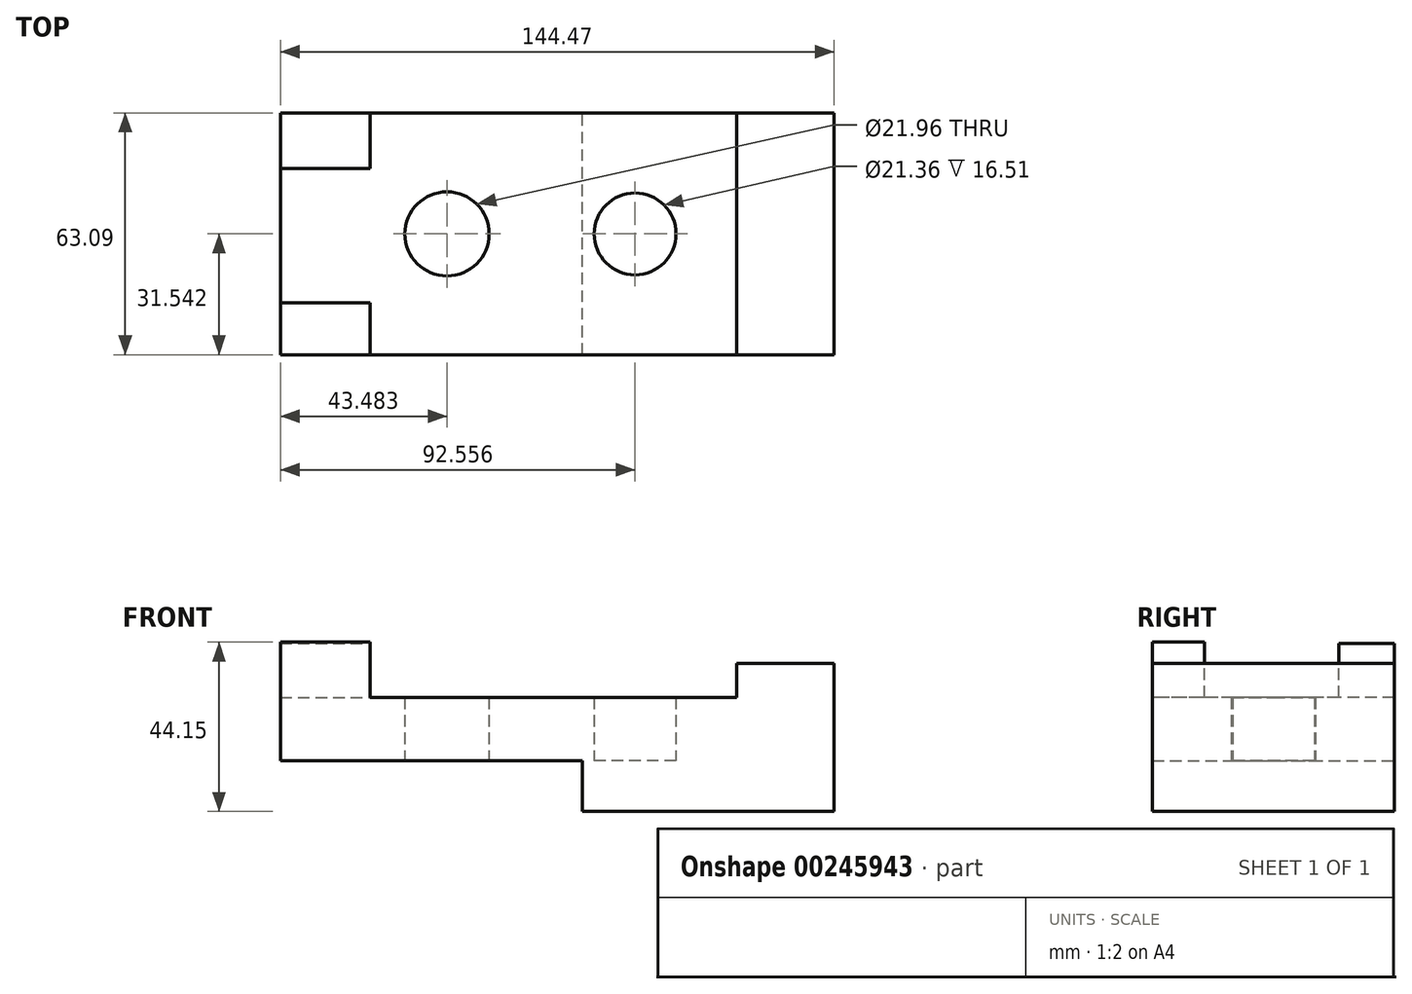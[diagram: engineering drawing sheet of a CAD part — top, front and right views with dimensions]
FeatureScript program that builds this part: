
annotation { "Feature Type Name" : "Feature", "Feature Type Description" : "" }
export const myFeature = defineFeature(function(context is Context, id is Id, definition is map)
    precondition{}
    {
        {
            var Q0;
            Q0=qCreatedBy(makeId("Top.planeOp"),FACE);
            var sketch = newSketch(context, id + "F0", { "sketchPlane" : qUnion([Q0])});
            skLineSegment(sketch, "E0.bottom", {"start": v(-55.47, 36.12) * mm, "end": v(40.23, 36.12) * mm});
            skLineSegment(sketch, "E0.top", {"start": v(-55.47, -26.97) * mm, "end": v(40.23, -26.97) * mm});
            skLineSegment(sketch, "E0.left", {"start": v(-55.47, 36.12) * mm, "end": v(-55.47, -26.97) * mm});
            skLineSegment(sketch, "E0.right", {"start": v(40.23, 36.12) * mm, "end": v(40.23, -26.97) * mm});
            skPoint(sketch, "E1.centerSnap0", {"position": v(-55.47, 4.57) * mm});
            skPoint(sketch, "E2.centerSnap0", {"position": v(40.23, 4.57) * mm});
            skCircle(sketch, "E3", {"center": v(-35.36, 4.57) * mm, "radius": 10.98 * mm});
            skCircle(sketch, "E4", {"center": v(13.72, 4.57) * mm, "radius": 10.68 * mm});
            skSolve(sketch);
        }
        {
            var Q0;
            Q0 = qSketchRegion(id + "F0", true);
            extrude(context, id + "F1", {"entities" : qUnion([Q0]), "depth" : 16.5 * mm});
        }
        {
            var Q0;
            Q0=makeQuery(id+"F1.opExtrude","SWEPT_FACE",FACE,{"disambiguationData":[OSD([sQuery(id+"F0.wireOp",EDGE,"E0.right")])]});
            var sketch = newSketch(context, id + "F2", { "sketchPlane" : qUnion([Q0])});
            skLineSegment(sketch, "E5.bottom", {"start": v(-26.97, 25.45) * mm, "end": v(36.12, 25.45) * mm});
            skLineSegment(sketch, "E5.top", {"start": v(-26.97, 0) * mm, "end": v(36.12, 0) * mm});
            skLineSegment(sketch, "E5.left", {"start": v(-26.97, 25.45) * mm, "end": v(-26.97, 0) * mm});
            skLineSegment(sketch, "E5.right", {"start": v(36.12, 25.45) * mm, "end": v(36.12, 0) * mm});
            skSolve(sketch);
        }
        {
            var Q0;
            Q0 = qSketchRegion(id + "F2", true);
            extrude(context, id + "F3", {"entities" : qUnion([Q0]), "operationType" : NewBodyOperationType.ADD, "depth" : 25.4 * mm});
        }
        {
            var Q0;
            Q0=makeQuery(id+"F3.boolean.opBoolean","MERGE",FACE,{"derivedFrom":[makeQuery(id+"F1.opExtrude","CAP_FACE",FACE,{"disambiguationData":[OSD([sQuery(id+"F0.wireOp",EDGE,"E0.bottom"),sQuery(id+"F0.wireOp",EDGE,"E0.top"),sQuery(id+"F0.wireOp",EDGE,"E0.left"),sQuery(id+"F0.wireOp",EDGE,"E0.right"),sQuery(id+"F0.wireOp",EDGE,"E3"),sQuery(id+"F0.wireOp",EDGE,"E4")])],"isStart":true}),makeQuery(id+"F3.opExtrude","SWEPT_FACE",FACE,{"disambiguationData":[OSD([sQuery(id+"F2.wireOp",EDGE,"E5.top")])]})]});
            var sketch = newSketch(context, id + "F4", { "sketchPlane" : qUnion([Q0])});
            skLineSegment(sketch, "E6.bottom", {"start": v(65.63, 26.97) * mm, "end": v(0, 26.97) * mm});
            skLineSegment(sketch, "E6.top", {"start": v(65.63, -36.12) * mm, "end": v(0, -36.12) * mm});
            skLineSegment(sketch, "E6.left", {"start": v(65.63, 26.97) * mm, "end": v(65.63, -36.12) * mm});
            skLineSegment(sketch, "E6.right", {"start": v(0, 26.97) * mm, "end": v(0, -36.12) * mm});
            skSolve(sketch);
        }
        {
            var Q0;
            Q0 = qSketchRegion(id + "F4", true);
            extrude(context, id + "F5", {"entities" : qUnion([Q0]), "operationType" : NewBodyOperationType.ADD, "depth" : 13.2 * mm});
        }
        {
            var Q0;
            Q0=makeQuery(id+"F1.opExtrude","SWEPT_FACE",FACE,{"disambiguationData":[OSD([sQuery(id+"F0.wireOp",EDGE,"E0.left")])]});
            var sketch = newSketch(context, id + "F6", { "sketchPlane" : qUnion([Q0])});
            skLineSegment(sketch, "E7.bottom", {"start": v(-36.12, 16.51) * mm, "end": v(26.97, 16.51) * mm});
            skLineSegment(sketch, "E7.top", {"start": v(-36.12, 0) * mm, "end": v(26.97, 0) * mm});
            skLineSegment(sketch, "E7.left", {"start": v(-36.12, 16.51) * mm, "end": v(-36.12, 0) * mm});
            skLineSegment(sketch, "E7.right", {"start": v(26.97, 16.51) * mm, "end": v(26.97, 0) * mm});
            skLineSegment(sketch, "E8.bottom", {"start": v(-36.12, 16.51) * mm, "end": v(-21.64, 16.51) * mm});
            skLineSegment(sketch, "E8.top", {"start": v(-36.12, 30.63) * mm, "end": v(-21.64, 30.63) * mm});
            skLineSegment(sketch, "E8.left", {"start": v(-36.12, 16.51) * mm, "end": v(-36.12, 30.63) * mm});
            skLineSegment(sketch, "E8.right", {"start": v(-21.64, 16.51) * mm, "end": v(-21.64, 30.63) * mm});
            skLineSegment(sketch, "E9.bottom", {"start": v(26.97, 16.51) * mm, "end": v(13.41, 16.51) * mm});
            skLineSegment(sketch, "E9.top", {"start": v(26.97, 30.94) * mm, "end": v(13.41, 30.94) * mm});
            skLineSegment(sketch, "E9.left", {"start": v(26.97, 16.51) * mm, "end": v(26.97, 30.94) * mm});
            skLineSegment(sketch, "E9.right", {"start": v(13.41, 16.51) * mm, "end": v(13.41, 30.94) * mm});
            skSolve(sketch);
        }
        {
            var Q0;
            Q0 = qSketchRegion(id + "F6", true);
            extrude(context, id + "F7", {"entities" : qUnion([Q0]), "operationType" : NewBodyOperationType.ADD, "depth" : 23.37 * mm});
        }
    });
